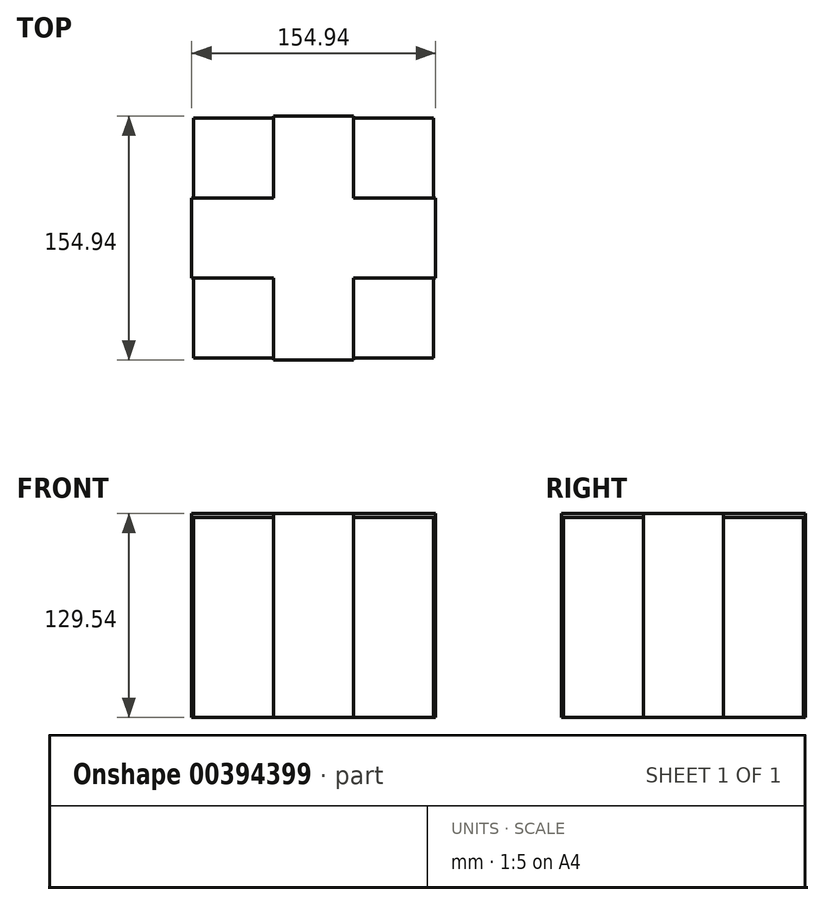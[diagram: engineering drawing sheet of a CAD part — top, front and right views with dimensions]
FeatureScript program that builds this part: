
annotation { "Feature Type Name" : "Feature", "Feature Type Description" : "" }
export const myFeature = defineFeature(function(context is Context, id is Id, definition is map)
    precondition{}
    {
        {
            var Q0;
            Q0=qCreatedBy(makeId("Top.planeOp"),FACE);
            var sketch = newSketch(context, id + "F0", { "sketchPlane" : qUnion([Q0])});
            skLineSegment(sketch, "E0.bottom", {"start": v(-76.2, 76.2) * mm, "end": v(76.2, 76.2) * mm});
            skLineSegment(sketch, "E0.top", {"start": v(-76.2, -76.2) * mm, "end": v(76.2, -76.2) * mm});
            skLineSegment(sketch, "E0.left", {"start": v(-76.2, 76.2) * mm, "end": v(-76.2, -76.2) * mm});
            skLineSegment(sketch, "E0.right", {"start": v(76.2, 76.2) * mm, "end": v(76.2, -76.2) * mm});
            skPoint(sketch, "E0.middle", {"position": v(0, 0) * mm});
            skLineSegment(sketch, "E1.bottom", {"start": v(-25.4, 77.47) * mm, "end": v(25.4, 77.47) * mm});
            skLineSegment(sketch, "E1.top", {"start": v(-25.4, 74.93) * mm, "end": v(25.4, 74.93) * mm});
            skLineSegment(sketch, "E1.left", {"start": v(-25.4, 77.47) * mm, "end": v(-25.4, 74.93) * mm});
            skLineSegment(sketch, "E1.right", {"start": v(25.4, 77.47) * mm, "end": v(25.4, 74.93) * mm});
            skPoint(sketch, "E1.middle", {"position": v(0, 76.2) * mm});
            skLineSegment(sketch, "E2.1.0", {"start": v(-77.47, -25.4) * mm, "end": v(-77.47, 25.4) * mm});
            skLineSegment(sketch, "E2.1.1", {"start": v(-77.47, -25.4) * mm, "end": v(-74.93, -25.4) * mm});
            skLineSegment(sketch, "E2.1.2", {"start": v(-77.47, 25.4) * mm, "end": v(-74.93, 25.4) * mm});
            skLineSegment(sketch, "E2.2.0", {"start": v(25.4, -77.47) * mm, "end": v(-25.4, -77.47) * mm});
            skLineSegment(sketch, "E2.2.1", {"start": v(25.4, -77.47) * mm, "end": v(25.4, -74.93) * mm});
            skLineSegment(sketch, "E2.2.2", {"start": v(-25.4, -77.47) * mm, "end": v(-25.4, -74.93) * mm});
            skLineSegment(sketch, "E3.1.3.0", {"start": v(77.47, 25.4) * mm, "end": v(77.47, -25.4) * mm});
            skLineSegment(sketch, "E3.3.3.0", {"start": v(77.47, 25.4) * mm, "end": v(74.93, 25.4) * mm});
            skLineSegment(sketch, "E3.6.3.0", {"start": v(77.47, -25.4) * mm, "end": v(74.93, -25.4) * mm});
            skSolve(sketch);
        }
        {
            var Q0;
            Q0=makeQuery(id+"F0.imprint","IMPRINT",FACE,{"disambiguationData":[TD([[makeQuery(id+"F0.imprint","IMPRINT",EDGE,{"derivedFrom":sQuery(id+"F0.wireOp",EDGE,"E0.bottom")}),-1.0]])]});
            var Q1;
            {var subQ5=sQuery(id+"F0.wireOp",EDGE,"E1.top");Q1=makeQuery(id+"F0.imprint","IMPRINT",FACE,{"disambiguationData":[TD([[makeQuery(id+"F0.imprint","IMPRINT",EDGE,{"derivedFrom":subQ5}),1.0]])]});}
            extrude(context, id + "F1", {"entities" : qUnion([Q0, Q1]), "depth" : 127 * mm});
        }
        {
            var Q0;
            {var subQ5=sQuery(id+"F0.wireOp",EDGE,"E3.1.3.0");Q0=makeQuery(id+"F0.imprint","IMPRINT",FACE,{"disambiguationData":[TD([[makeQuery(id+"F0.imprint","IMPRINT",EDGE,{"derivedFrom":subQ5}),-1.0]])]});}
            var Q1;
            {var subQ5=sQuery(id+"F0.wireOp",EDGE,"E1.bottom");Q1=makeQuery(id+"F0.imprint","IMPRINT",FACE,{"disambiguationData":[TD([[makeQuery(id+"F0.imprint","IMPRINT",EDGE,{"derivedFrom":subQ5}),-1.0]])]});}
            var Q2;
            {var subQ5=sQuery(id+"F0.wireOp",EDGE,"E2.2.0");Q2=makeQuery(id+"F0.imprint","IMPRINT",FACE,{"disambiguationData":[TD([[makeQuery(id+"F0.imprint","IMPRINT",EDGE,{"derivedFrom":subQ5}),-1.0]])]});}
            var Q3;
            {var subQ5=sQuery(id+"F0.wireOp",EDGE,"E2.1.0");Q3=makeQuery(id+"F0.imprint","IMPRINT",FACE,{"disambiguationData":[TD([[makeQuery(id+"F0.imprint","IMPRINT",EDGE,{"derivedFrom":subQ5}),-1.0]])]});}
            extrude(context, id + "F2", {"entities" : qUnion([Q0, Q1, Q2, Q3]), "depth" : 129.54 * mm});
        }
        {
            var Q0;
            Q0=makeQuery(id+"F2.opExtrude","SWEPT_FACE",FACE,{"disambiguationData":[OSD([sQuery(id+"F0.wireOp",EDGE,"E0.bottom")])]});
            extrude(context, id + "F3", {"entities" : qUnion([Q0]), "operationType" : NewBodyOperationType.ADD, "depth" : 152.4 * mm});
        }
        {
            var Q0;
            Q0=makeQuery(id+"F2.opExtrude","SWEPT_FACE",FACE,{"disambiguationData":[OSD([sQuery(id+"F0.wireOp",EDGE,"E0.right")])]});
            extrude(context, id + "F4", {"entities" : qUnion([Q0]), "operationType" : NewBodyOperationType.ADD, "depth" : 152.4 * mm});
        }
    });
